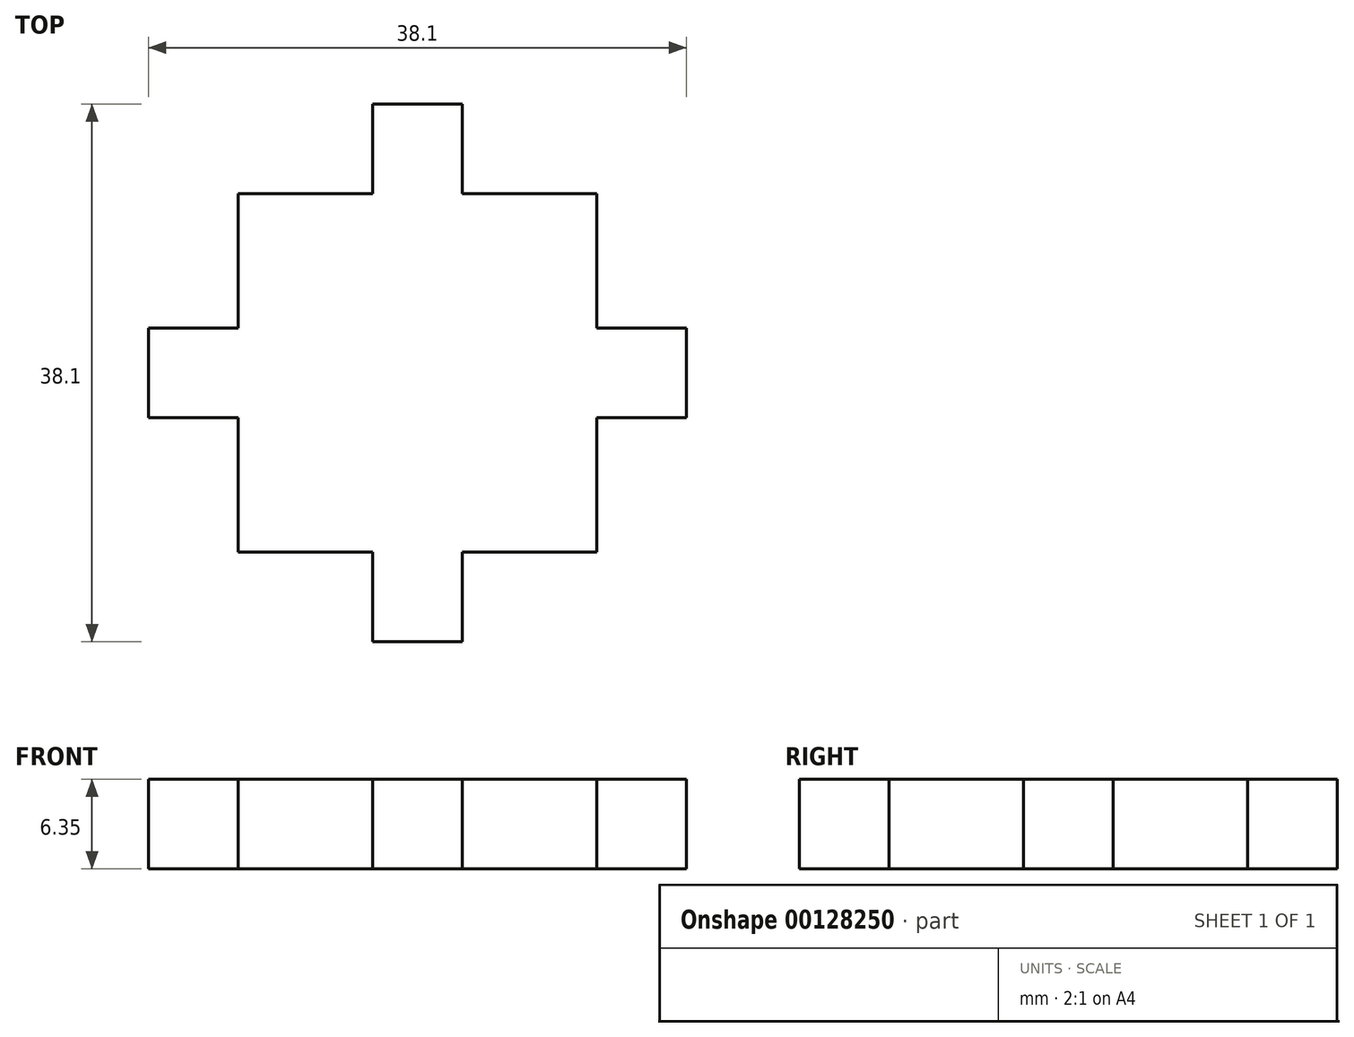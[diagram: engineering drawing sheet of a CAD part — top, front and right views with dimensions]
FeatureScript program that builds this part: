
annotation { "Feature Type Name" : "Feature", "Feature Type Description" : "" }
export const myFeature = defineFeature(function(context is Context, id is Id, definition is map)
    precondition{}
    {
        {
            var Q0;
            Q0=qCreatedBy(makeId("Top.planeOp"),FACE);
            var sketch = newSketch(context, id + "F0", { "sketchPlane" : qUnion([Q0])});
            skLineSegment(sketch, "E0.bottom", {"start": v(0, 0) * mm, "end": v(25.4, 0) * mm});
            skLineSegment(sketch, "E0.top", {"start": v(0, -25.4) * mm, "end": v(25.4, -25.4) * mm});
            skLineSegment(sketch, "E0.left", {"start": v(0, 0) * mm, "end": v(0, -25.4) * mm});
            skLineSegment(sketch, "E0.right", {"start": v(25.4, 0) * mm, "end": v(25.4, -25.4) * mm});
            skLineSegment(sketch, "E1.bottom", {"start": v(9.53, 0) * mm, "end": v(15.88, 0) * mm});
            skLineSegment(sketch, "E1.top", {"start": v(9.53, 6.35) * mm, "end": v(15.88, 6.35) * mm});
            skLineSegment(sketch, "E1.left", {"start": v(9.53, 0) * mm, "end": v(9.53, 6.35) * mm});
            skLineSegment(sketch, "E1.right", {"start": v(15.88, 0) * mm, "end": v(15.88, 6.35) * mm});
            skLineSegment(sketch, "E2.bottom", {"start": v(25.4, -9.52) * mm, "end": v(31.75, -9.52) * mm});
            skLineSegment(sketch, "E2.top", {"start": v(25.4, -15.88) * mm, "end": v(31.75, -15.88) * mm});
            skLineSegment(sketch, "E2.left", {"start": v(25.4, -9.52) * mm, "end": v(25.4, -15.88) * mm});
            skLineSegment(sketch, "E2.right", {"start": v(31.75, -9.52) * mm, "end": v(31.75, -15.88) * mm});
            skLineSegment(sketch, "E3.bottom", {"start": v(9.53, -25.4) * mm, "end": v(15.88, -25.4) * mm});
            skLineSegment(sketch, "E3.top", {"start": v(9.53, -31.75) * mm, "end": v(15.88, -31.75) * mm});
            skLineSegment(sketch, "E3.left", {"start": v(9.53, -25.4) * mm, "end": v(9.53, -31.75) * mm});
            skLineSegment(sketch, "E3.right", {"start": v(15.88, -25.4) * mm, "end": v(15.88, -31.75) * mm});
            skLineSegment(sketch, "E4.bottom", {"start": v(0, -15.88) * mm, "end": v(-6.35, -15.88) * mm});
            skLineSegment(sketch, "E4.top", {"start": v(0, -9.53) * mm, "end": v(-6.35, -9.53) * mm});
            skLineSegment(sketch, "E4.left", {"start": v(0, -15.88) * mm, "end": v(0, -9.53) * mm});
            skLineSegment(sketch, "E4.right", {"start": v(-6.35, -15.88) * mm, "end": v(-6.35, -9.53) * mm});
            skSolve(sketch);
        }
        {
            var Q0;
            Q0 = qSketchRegion(id + "F0", true);
            extrude(context, id + "F1", {"entities" : qUnion([Q0]), "depth" : 6.35 * mm});
        }
    });
